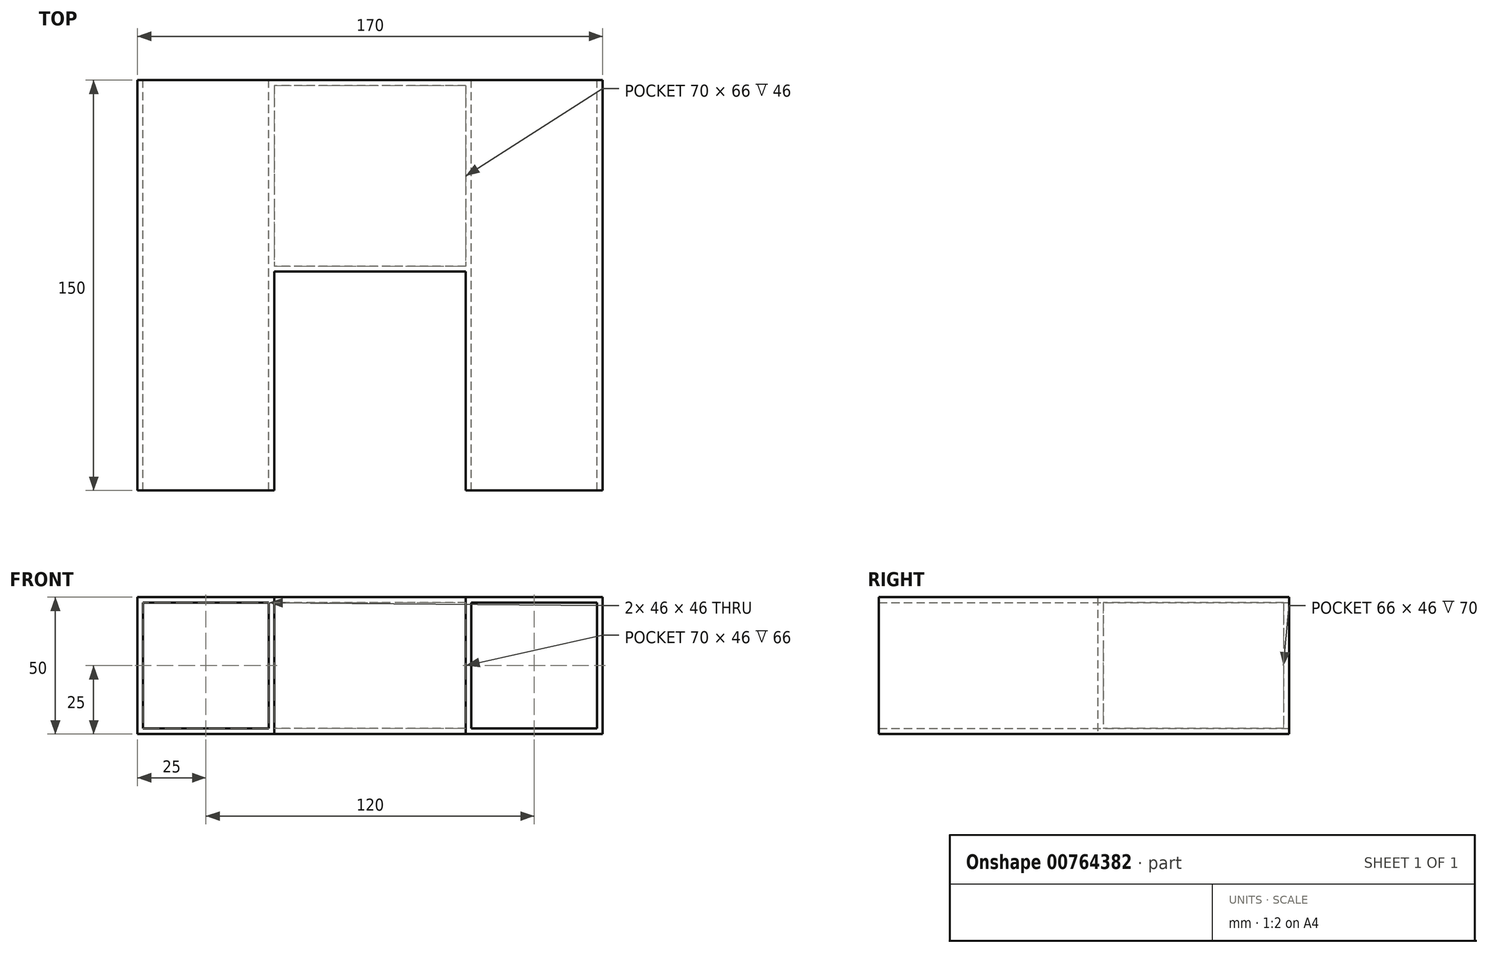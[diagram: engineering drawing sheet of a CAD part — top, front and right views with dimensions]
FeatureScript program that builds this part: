
annotation { "Feature Type Name" : "Feature", "Feature Type Description" : "" }
export const myFeature = defineFeature(function(context is Context, id is Id, definition is map)
    precondition{}
    {
        {
            var Q0;
            Q0=qCreatedBy(makeId("Front.planeOp"),FACE);
            var sketch = newSketch(context, id + "F0", { "sketchPlane" : qUnion([Q0])});
            skLineSegment(sketch, "E0.bottom", {"start": v(-25, 25) * mm, "end": v(25, 25) * mm});
            skLineSegment(sketch, "E0.top", {"start": v(-25, -25) * mm, "end": v(25, -25) * mm});
            skLineSegment(sketch, "E0.left", {"start": v(-25, 25) * mm, "end": v(-25, -25) * mm});
            skLineSegment(sketch, "E0.right", {"start": v(25, 25) * mm, "end": v(25, -25) * mm});
            skLineSegment(sketch, "E1.0", {"start": v(-23, 23) * mm, "end": v(-23, -23) * mm});
            skLineSegment(sketch, "E1.1", {"start": v(-23, 23) * mm, "end": v(23, 23) * mm});
            skLineSegment(sketch, "E1.2", {"start": v(23, 23) * mm, "end": v(23, -23) * mm});
            skLineSegment(sketch, "E1.3", {"start": v(-23, -23) * mm, "end": v(23, -23) * mm});
            skSolve(sketch);
        }
        {
            var Q0;
            Q0=makeQuery(id+"F0.imprint","IMPRINT",FACE,{"disambiguationData":[TD([[makeQuery(id+"F0.imprint","IMPRINT",EDGE,{"derivedFrom":sQuery(id+"F0.wireOp",EDGE,"E0.bottom")}),-1.0]])]});
            extrude(context, id + "F1", {"entities" : qUnion([Q0]), "depth" : 150 * mm, "offsetDistance" : 25 * mm, "symmetric" : true});
        }
        {
            var Q0;
            Q0=makeQuery(id+"F1.opExtrude","SWEPT_FACE",FACE,{"disambiguationData":[OSD([sQuery(id+"F0.wireOp",EDGE,"E0.right")])]});
            var sketch = newSketch(context, id + "F2", { "sketchPlane" : qUnion([Q0])});
            skLineSegment(sketch, "E2.bottom", {"start": v(75, 25) * mm, "end": v(5, 25) * mm});
            skLineSegment(sketch, "E2.top", {"start": v(75, -25) * mm, "end": v(5, -25) * mm});
            skLineSegment(sketch, "E2.left", {"start": v(75, 25) * mm, "end": v(75, -25) * mm});
            skLineSegment(sketch, "E2.right", {"start": v(5, 25) * mm, "end": v(5, -25) * mm});
            skLineSegment(sketch, "E3.0", {"start": v(73, 23) * mm, "end": v(7, 23) * mm});
            skLineSegment(sketch, "E3.1", {"start": v(73, 23) * mm, "end": v(73, -23) * mm});
            skLineSegment(sketch, "E3.2", {"start": v(73, -23) * mm, "end": v(7, -23) * mm});
            skLineSegment(sketch, "E3.3", {"start": v(7, 23) * mm, "end": v(7, -23) * mm});
            skSolve(sketch);
        }
        {
            var Q0;
            Q0=makeQuery(id+"F2.imprint","IMPRINT",FACE,{"disambiguationData":[TD([[makeQuery(id+"F2.imprint","IMPRINT",EDGE,{"derivedFrom":sQuery(id+"F2.wireOp",EDGE,"E2.bottom")}),-1.0]])]});
            extrude(context, id + "F3", {"entities" : qUnion([Q0]), "operationType" : NewBodyOperationType.ADD, "depth" : 35 * mm, "offsetDistance" : 25 * mm});
        }
        {
            var Q0;
            Q0=makeQuery(id+"F3.opExtrude","CAP_FACE",FACE,{"disambiguationData":[OSD([sQuery(id+"F2.wireOp",EDGE,"E2.bottom"),sQuery(id+"F2.wireOp",EDGE,"E2.top"),sQuery(id+"F2.wireOp",EDGE,"E2.left"),sQuery(id+"F2.wireOp",EDGE,"E2.right"),sQuery(id+"F2.wireOp",EDGE,"E3.0"),sQuery(id+"F2.wireOp",EDGE,"E3.1"),sQuery(id+"F2.wireOp",EDGE,"E3.2"),sQuery(id+"F2.wireOp",EDGE,"E3.3")])],"isStart":false});
            cPlane(context, id + "F4", {"entities" : qUnion([Q0]), "cplaneType" : CPlaneType.OFFSET, "offset" : 0 * mm, "width" : 150 * mm, "height" : 150 * mm});
        }
        {
            var Q0;
            Q0=makeQuery(id+"F1.opExtrude","SWEPT_BODY",BODY,{"disambiguationData":[OSD([sQuery(id+"F0.wireOp",EDGE,"E0.bottom"),sQuery(id+"F0.wireOp",EDGE,"E0.top"),sQuery(id+"F0.wireOp",EDGE,"E0.left"),sQuery(id+"F0.wireOp",EDGE,"E0.right"),sQuery(id+"F0.wireOp",EDGE,"E1.0"),sQuery(id+"F0.wireOp",EDGE,"E1.1"),sQuery(id+"F0.wireOp",EDGE,"E1.2"),sQuery(id+"F0.wireOp",EDGE,"E1.3")])]});
            var Q1;
            Q1=qCreatedBy(id+"F4.planeOp",FACE);
            mirror(context, id + "F5", {"operationType" : NewBodyOperationType.ADD, "entities" : qUnion([Q0]), "mirrorPlane" : qUnion([Q1])});
        }
    });
